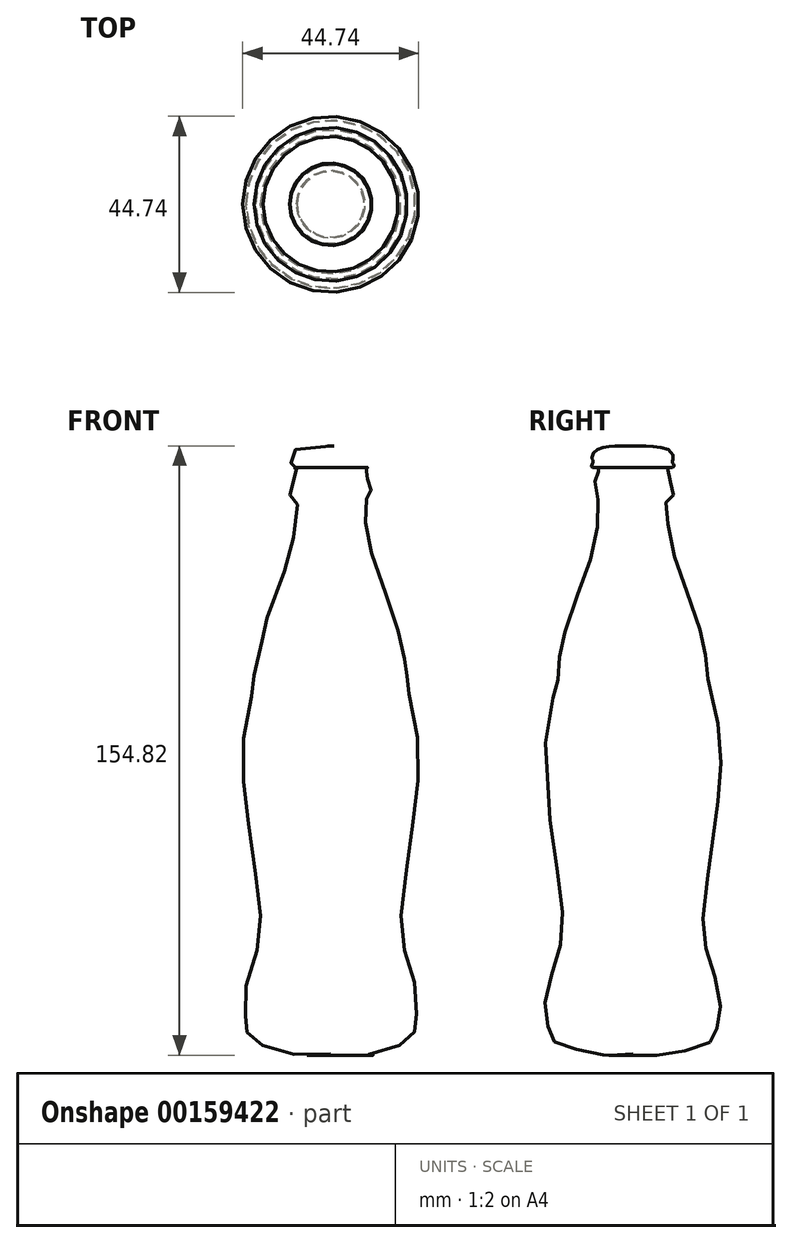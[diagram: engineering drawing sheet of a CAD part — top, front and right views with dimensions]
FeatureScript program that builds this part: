
annotation { "Feature Type Name" : "Feature", "Feature Type Description" : "" }
export const myFeature = defineFeature(function(context is Context, id is Id, definition is map)
    precondition{}
    {
        {
            var Q0;
            Q0=qCreatedBy(makeId("Front.planeOp"),FACE);
            var sketch = newSketch(context, id + "F0", { "sketchPlane" : qUnion([Q0])});
            skLineSegment(sketch, "E0", {"start": v(0, 77.6) * mm, "end": v(0, -76.88) * mm});
            skFitSpline(sketch, "E1", {"points": [v(0, -76.88) * mm, v(-10.23, -76.88) * mm, v(-17.72, -74.58) * mm, v(-20.46, -73.21) * mm, v(-21.51, -69.27) * mm, v(-21.35, -68.38) * mm, v(-22.24, -65) * mm, v(-20.3, -55.65) * mm, v(-17.88, -46.14) * mm, v(-18.53, -35.26) * mm, v(-21.07, -16.78) * mm, v(-22.36, -3.32) * mm, v(-20.77, 11.66) * mm, v(-19.02, 18.36) * mm, v(-19.47, 19.42) * mm, v(-17.27, 28.85) * mm, v(-17.12, 30.83) * mm, v(-11.87, 45.58) * mm, v(-9.36, 54.78) * mm, v(-8.45, 62.77) * mm, v(-8.75, 63.83) * mm, v(-9.97, 64.82) * mm, v(-10.42, 65.5) * mm, v(-8.67, 71.9) * mm, v(-9.36, 72.05) * mm, v(-10.5, 72.43) * mm, v(-10.04, 73.5) * mm, v(-10.35, 74.48) * mm, v(-9.28, 76.46) * mm, v(0, 77.6) * mm], "startDerivative": vector(-216.9, -18.44) * mm, "endDerivative": vector(246.81, -0.4) * mm});
            skSolve(sketch);
        }
        {
            var Q0;
            Q0=makeQuery(id+"F0.imprint","IMPRINT",FACE,{"disambiguationData":[TD([[makeQuery(id+"F0.imprint","IMPRINT",EDGE,{"derivedFrom":sQuery(id+"F0.wireOp",EDGE,"E0")}),-1.0]])]});
            var Q1;
            Q1=sQuery(id+"F0.wireOp",EDGE,"E0");
            revolve(context, id + "F1", {"entities" : qUnion([Q0]), "axis" : qUnion([Q1]), "revolveType" : RevolveType.FULL});
        }
    });
